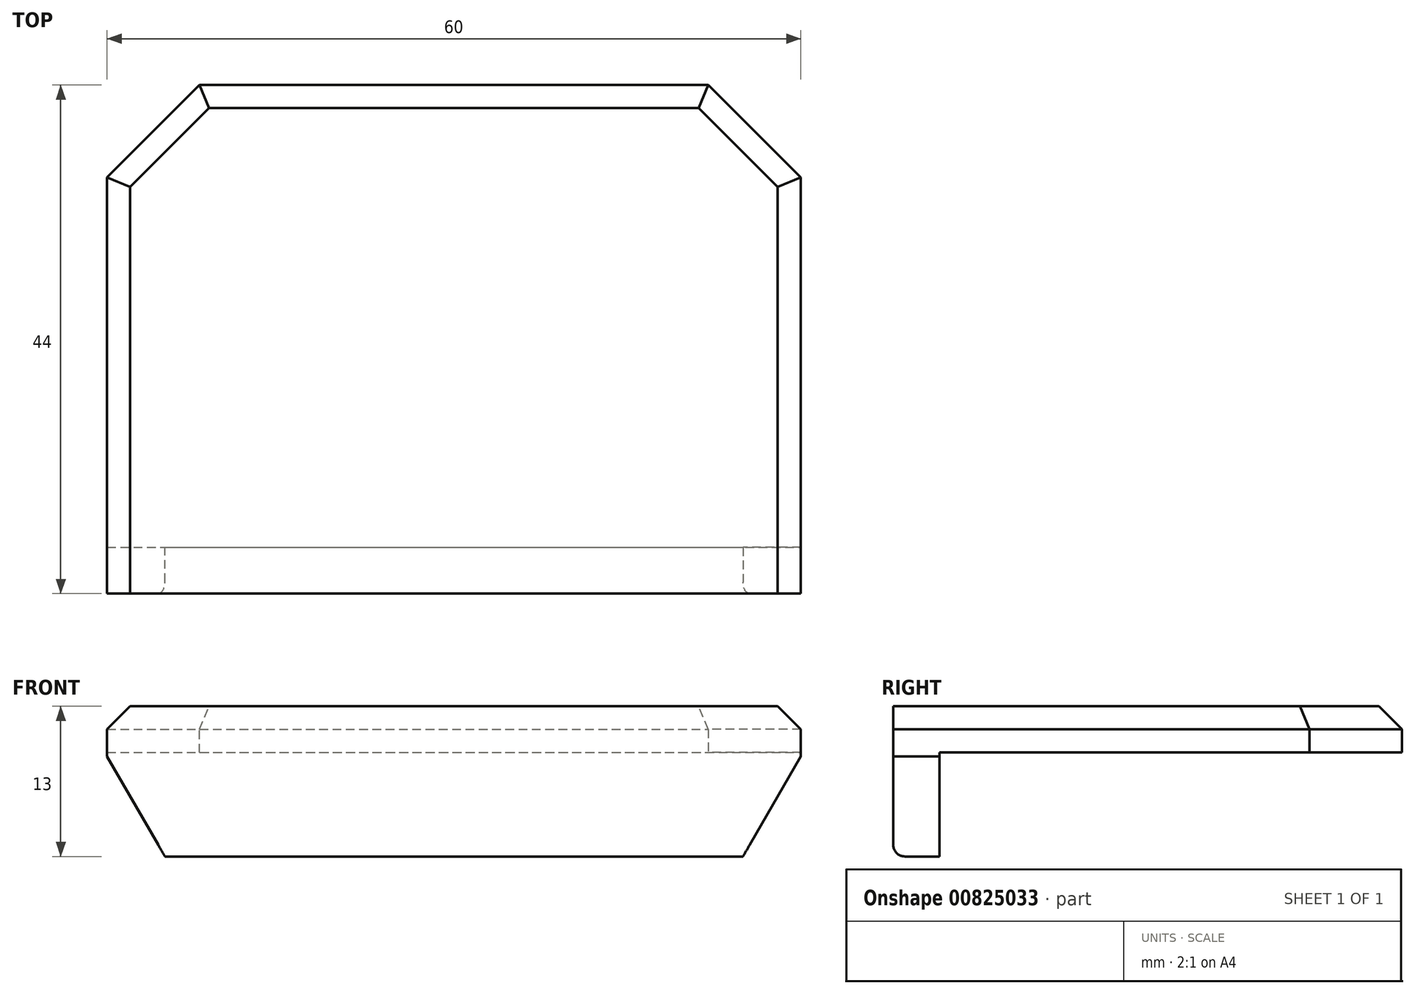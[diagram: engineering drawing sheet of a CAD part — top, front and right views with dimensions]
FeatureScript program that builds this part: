
annotation { "Feature Type Name" : "Feature", "Feature Type Description" : "" }
export const myFeature = defineFeature(function(context is Context, id is Id, definition is map)
    precondition{}
    {
        {
            var Q0;
            Q0=qCreatedBy(makeId("Top.planeOp"),FACE);
            var sketch = newSketch(context, id + "F0", { "sketchPlane" : qUnion([Q0])});
            skLineSegment(sketch, "E0.bottom", {"start": v(-30, 40) * mm, "end": v(30, 40) * mm});
            skLineSegment(sketch, "E0.top", {"start": v(-30, 0) * mm, "end": v(30, 0) * mm});
            skLineSegment(sketch, "E0.left", {"start": v(-30, 40) * mm, "end": v(-30, 0) * mm});
            skLineSegment(sketch, "E0.right", {"start": v(30, 40) * mm, "end": v(30, 0) * mm});
            skSolve(sketch);
        }
        {
            var Q0;
            Q0=makeQuery(id+"F0.imprint","IMPRINT",FACE,{"disambiguationData":[TD([[makeQuery(id+"F0.imprint","IMPRINT",EDGE,{"derivedFrom":sQuery(id+"F0.wireOp",EDGE,"E0.bottom")}),-1.0]])]});
            extrude(context, id + "F1", {"entities" : qUnion([Q0]), "depth" : 5 * mm, "offsetDistance" : 25 * mm});
        }
        {
            var Q0;
            Q0=makeQuery(id+"F1.opExtrude","SWEPT_EDGE",EDGE,{"disambiguationData":[OSD([sQuery(id+"F0.wireOp",EDGE,"E0.bottom"),sQuery(id+"F0.wireOp",EDGE,"E0.right")])]});
            var Q1;
            Q1=makeQuery(id+"F1.opExtrude","SWEPT_EDGE",EDGE,{"disambiguationData":[OSD([sQuery(id+"F0.wireOp",EDGE,"E0.bottom"),sQuery(id+"F0.wireOp",EDGE,"E0.left")])]});
            chamfer(context, id + "F2", {"entities" : qUnion([Q0, Q1]), "width" : 8 * mm, "tangentPropagation" : true});
        }
        {
            var Q0;
            Q0=makeQuery(id+"F1.opExtrude","SWEPT_FACE",FACE,{"disambiguationData":[OSD([sQuery(id+"F0.wireOp",EDGE,"E0.top")])]});
            var sketch = newSketch(context, id + "F3", { "sketchPlane" : qUnion([Q0])});
            skLineSegment(sketch, "E1.bottom", {"start": v(-30, 5) * mm, "end": v(30, 5) * mm});
            skLineSegment(sketch, "E1.top", {"start": v(-30, -9) * mm, "end": v(30, -9) * mm});
            skLineSegment(sketch, "E1.left", {"start": v(-30, 5) * mm, "end": v(-30, -9) * mm});
            skLineSegment(sketch, "E1.right", {"start": v(30, 5) * mm, "end": v(30, -9) * mm});
            skSolve(sketch);
        }
        {
            var Q0;
            {var subQ0=sQuery(id+"F3.wireOp",EDGE,"E1.top");Q0=makeQuery(id+"F3.imprint","IMPRINT",FACE,{"disambiguationData":[TD([[makeQuery(id+"F3.imprint","IMPRINT",EDGE,{"derivedFrom":subQ0}),1.0]])]});}
            var Q1;
            {var subQ0=sQuery(id+"F3.wireOp",EDGE,"E1.bottom");Q1=makeQuery(id+"F3.imprint","IMPRINT",FACE,{"disambiguationData":[TD([[makeQuery(id+"F3.imprint","IMPRINT",EDGE,{"derivedFrom":subQ0}),-1.0]])]});}
            extrude(context, id + "F4", {"entities" : qUnion([Q0, Q1]), "operationType" : NewBodyOperationType.ADD, "depth" : 4 * mm, "offsetDistance" : 25 * mm});
        }
        {
            var Q0;
            Q0=makeQuery(id+"F4.boolean.opBoolean","MERGE",EDGE,{"derivedFrom":[makeQuery(id+"F1.opExtrude","CAP_EDGE",EDGE,{"disambiguationData":[OSD([sQuery(id+"F0.wireOp",EDGE,"E0.left")])],"isStart":false}),makeQuery(id+"F4.opExtrude","SWEPT_EDGE",EDGE,{"disambiguationData":[OSD([sQuery(id+"F3.wireOp",EDGE,"E1.bottom"),sQuery(id+"F3.wireOp",EDGE,"E1.left")])]})]});
            var Q1;
            Q1=makeQuery(id+"F4.boolean.opBoolean","MERGE",EDGE,{"derivedFrom":[makeQuery(id+"F1.opExtrude","CAP_EDGE",EDGE,{"disambiguationData":[OSD([sQuery(id+"F0.wireOp",EDGE,"E0.right")])],"isStart":false}),makeQuery(id+"F4.opExtrude","SWEPT_EDGE",EDGE,{"disambiguationData":[OSD([sQuery(id+"F3.wireOp",EDGE,"E1.bottom"),sQuery(id+"F3.wireOp",EDGE,"E1.right")])]})]});
            var Q2;
            Q2=makeQuery(id+"F1.opExtrude","CAP_EDGE",EDGE,{"disambiguationData":[OSD([sQuery(id+"F0.wireOp",EDGE,"E0.bottom")])],"isStart":false});
            var Q3;
            {var subQ0=sQuery(id+"F0.wireOp",EDGE,"E0.right");var subQ1=sQuery(id+"F0.wireOp",EDGE,"E0.bottom");Q3=makeQuery(id+"F2.opChamfer","BLEND_EDGE",EDGE,{"blendedFrom":[makeQuery(id+"F1.opExtrude","SWEPT_EDGE",EDGE,{"disambiguationData":[OSD([subQ1,subQ0])]}),makeQuery(id+"F1.opExtrude","CAP_FACE",FACE,{"disambiguationData":[OSD([subQ1,sQuery(id+"F0.wireOp",EDGE,"E0.top"),sQuery(id+"F0.wireOp",EDGE,"E0.left"),subQ0])],"isStart":false})],"blendedInto":[makeQuery(id+"F1.opExtrude","CAP_FACE",FACE,{"disambiguationData":[OSD([subQ1,sQuery(id+"F0.wireOp",EDGE,"E0.top"),sQuery(id+"F0.wireOp",EDGE,"E0.left"),subQ0])],"isStart":false})]});}
            var Q4;
            {var subQ0=sQuery(id+"F0.wireOp",EDGE,"E0.left");var subQ1=sQuery(id+"F0.wireOp",EDGE,"E0.bottom");Q4=makeQuery(id+"F2.opChamfer","BLEND_EDGE",EDGE,{"blendedFrom":[makeQuery(id+"F1.opExtrude","SWEPT_EDGE",EDGE,{"disambiguationData":[OSD([subQ1,subQ0])]}),makeQuery(id+"F1.opExtrude","CAP_FACE",FACE,{"disambiguationData":[OSD([subQ1,sQuery(id+"F0.wireOp",EDGE,"E0.top"),subQ0,sQuery(id+"F0.wireOp",EDGE,"E0.right")])],"isStart":false})],"blendedInto":[makeQuery(id+"F1.opExtrude","CAP_FACE",FACE,{"disambiguationData":[OSD([subQ1,sQuery(id+"F0.wireOp",EDGE,"E0.top"),subQ0,sQuery(id+"F0.wireOp",EDGE,"E0.right")])],"isStart":false})]});}
            chamfer(context, id + "F5", {"entities" : qUnion([Q0, Q1, Q2, Q3, Q4]), "width" : 3 * mm, "tangentPropagation" : true});
        }
        {
            var Q0;
            Q0=makeQuery(id+"F4.opExtrude","SWEPT_EDGE",EDGE,{"disambiguationData":[OSD([sQuery(id+"F3.wireOp",EDGE,"E1.top"),sQuery(id+"F3.wireOp",EDGE,"E1.left")])]});
            var Q1;
            Q1=makeQuery(id+"F4.opExtrude","SWEPT_EDGE",EDGE,{"disambiguationData":[OSD([sQuery(id+"F3.wireOp",EDGE,"E1.top"),sQuery(id+"F3.wireOp",EDGE,"E1.right")])]});
            chamfer(context, id + "F6", {"entities" : qUnion([Q0, Q1]), "chamferType" : ChamferType.OFFSET_ANGLE, "width" : 5 * mm, "oppositeDirection" : false, "angle" : 60 * degree, "tangentPropagation" : true});
        }
        {
            var Q0;
            Q0=makeQuery(id+"F4.opExtrude","CAP_EDGE",EDGE,{"disambiguationData":[OSD([sQuery(id+"F3.wireOp",EDGE,"E1.top")])],"isStart":false});
            fillet(context, id + "F7", {"entities" : qUnion([Q0]), "radius" : 1 * mm, "tangentPropagation" : true, "allowEdgeOverflow" : false});
        }
        {
            var Q0;
            Q0=makeQuery(id+"F4.boolean.opBoolean","MERGE",FACE,{"derivedFrom":[makeQuery(id+"F1.opExtrude","CAP_FACE",FACE,{"disambiguationData":[OSD([sQuery(id+"F0.wireOp",EDGE,"E0.bottom"),sQuery(id+"F0.wireOp",EDGE,"E0.top"),sQuery(id+"F0.wireOp",EDGE,"E0.left"),sQuery(id+"F0.wireOp",EDGE,"E0.right")])],"isStart":false}),makeQuery(id+"F4.opExtrude","SWEPT_FACE",FACE,{"disambiguationData":[OSD([sQuery(id+"F3.wireOp",EDGE,"E1.bottom")])]})]});
            var sketch = newSketch(context, id + "F8", { "sketchPlane" : qUnion([Q0])});
            skLineSegment(sketch, "E2.bottom", {"start": v(-44.48, -7) * mm, "end": v(41, -7) * mm});
            skLineSegment(sketch, "E2.top", {"start": v(-44.48, 55.54) * mm, "end": v(41, 55.54) * mm});
            skLineSegment(sketch, "E2.left", {"start": v(-44.48, -7) * mm, "end": v(-44.48, 55.54) * mm});
            skLineSegment(sketch, "E2.right", {"start": v(41, -7) * mm, "end": v(41, 55.54) * mm});
            skSolve(sketch);
        }
        {
            var Q0;
            Q0=makeQuery(id+"F8.imprint","IMPRINT",FACE,{"disambiguationData":[TD([[makeQuery(id+"F8.imprint","IMPRINT",EDGE,{"derivedFrom":sQuery(id+"F8.wireOp",EDGE,"E2.bottom")}),1.0]])]});
            var Q1;
            {var subQ0=sQuery(id+"F3.wireOp",EDGE,"E1.bottom");Q1=makeQuery(id+"F8.imprint","IMPRINT",FACE,{"disambiguationData":[TD([[makeQuery(id+"F8.imprint","IMPRINT",EDGE,{"derivedFrom":makeQuery(id+"F4.opExtrude","CAP_EDGE",EDGE,{"disambiguationData":[OSD([subQ0])],"isStart":false})}),1.0]])]});}
            extrude(context, id + "F9", {"entities" : qUnion([Q0, Q1]), "operationType" : NewBodyOperationType.REMOVE, "oppositeDirection" : true, "depth" : 1 * mm, "offsetDistance" : 25 * mm});
        }
    });
